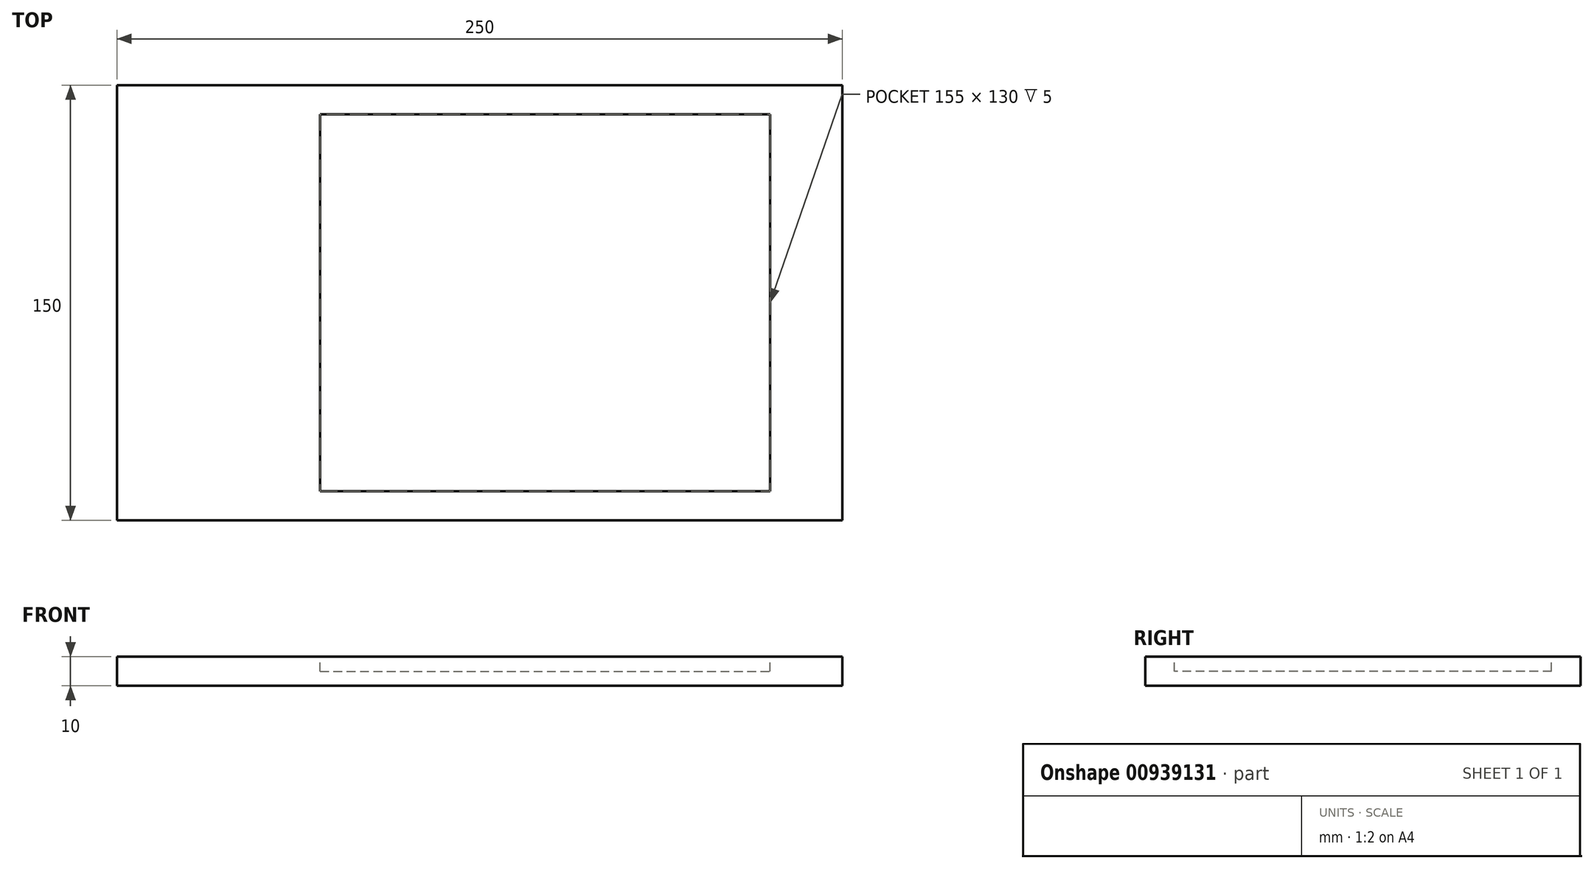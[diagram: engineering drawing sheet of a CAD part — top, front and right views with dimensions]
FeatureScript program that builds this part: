
annotation { "Feature Type Name" : "Feature", "Feature Type Description" : "" }
export const myFeature = defineFeature(function(context is Context, id is Id, definition is map)
    precondition{}
    {
        {
            var Q0;
            Q0=qCreatedBy(makeId("Top.planeOp"),FACE);
            var sketch = newSketch(context, id + "F0", { "sketchPlane" : qUnion([Q0])});
            skLineSegment(sketch, "E0.bottom", {"start": v(125, 75) * mm, "end": v(-125, 75) * mm});
            skLineSegment(sketch, "E0.top", {"start": v(125, -75) * mm, "end": v(-125, -75) * mm});
            skLineSegment(sketch, "E0.left", {"start": v(125, 75) * mm, "end": v(125, -75) * mm});
            skLineSegment(sketch, "E0.right", {"start": v(-125, 75) * mm, "end": v(-125, -75) * mm});
            skPoint(sketch, "E0.middle", {"position": v(0, 0) * mm});
            skLineSegment(sketch, "E1.bottom", {"start": v(-55, 65) * mm, "end": v(100, 65) * mm});
            skLineSegment(sketch, "E1.top", {"start": v(-55, -65) * mm, "end": v(100, -65) * mm});
            skLineSegment(sketch, "E1.left", {"start": v(-55, 65) * mm, "end": v(-55, -65) * mm});
            skLineSegment(sketch, "E1.right", {"start": v(100, 65) * mm, "end": v(100, -65) * mm});
            skLineSegment(sketch, "E2", {"start": v(-125, 0) * mm, "end": v(-55, 0) * mm, "construction": true});
            skLineSegment(sketch, "E3", {"start": v(100, 0) * mm, "end": v(125, 0) * mm, "construction": true});
            skLineSegment(sketch, "E4", {"start": v(4.41, -65) * mm, "end": v(4.41, -75) * mm, "construction": true});
            skLineSegment(sketch, "E5", {"start": v(0, 65) * mm, "end": v(0, 75) * mm, "construction": true});
            skPoint(sketch, "E5.startSnap0", {"position": v(0, 75) * mm});
            skSolve(sketch);
        }
        {
            var Q0;
            Q0=makeQuery(id+"F0.imprint","IMPRINT",FACE,{"disambiguationData":[TD([[makeQuery(id+"F0.imprint","IMPRINT",EDGE,{"derivedFrom":sQuery(id+"F0.wireOp",EDGE,"E0.bottom")}),1.0]])]});
            var Q1;
            Q1=makeQuery(id+"F0.imprint","IMPRINT",FACE,{"disambiguationData":[TD([[makeQuery(id+"F0.imprint","IMPRINT",EDGE,{"derivedFrom":sQuery(id+"F0.wireOp",EDGE,"E1.bottom")}),-1.0]])]});
            extrude(context, id + "F1", {"entities" : qUnion([Q0, Q1]), "oppositeDirection" : true, "depth" : 10 * mm, "offsetDistance" : 25 * mm});
        }
        {
            var Q0;
            Q0=makeQuery(id+"F0.imprint","IMPRINT",FACE,{"disambiguationData":[TD([[makeQuery(id+"F0.imprint","IMPRINT",EDGE,{"derivedFrom":sQuery(id+"F0.wireOp",EDGE,"E1.bottom")}),-1.0]])]});
            extrude(context, id + "F2", {"entities" : qUnion([Q0]), "operationType" : NewBodyOperationType.REMOVE, "oppositeDirection" : true, "depth" : 5 * mm, "offsetDistance" : 25 * mm});
        }
    });
